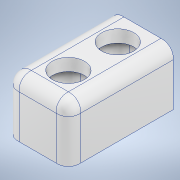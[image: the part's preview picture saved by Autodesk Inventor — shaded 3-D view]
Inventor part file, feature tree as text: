
AUTODESK INVENTOR PART (.ipt)
format: ipt  version: 2021 (Build 250183000, 183)  size: 1,595,392 bytes
history: native  units: in
note: dims shown in document units (in); Inventor stores cm internally (conversion verified against a paired STEP export)
features: extrude x9, other x7, fillet x2, sketch x1
ambient origin geometry x8: Origin, YZ Plane, XZ Plane, XY Plane, X Axis, Y Axis, Z Axis, Center Point
bodies: Body1 (feature_tree)
feature tree (19):
  extrude  "Base"  Depth=1.9685in
  extrude  "Top"  Depth=1.7717in TaperAngle=0.0deg
  extrude  "Walls"  Depth=1.1811in
  fillet  "Outer"  Radius=1.1811in
  extrude  "Wire"  Depth=1.1811in
  extrude  "Wall Holes"  Depth=1.1811in
  extrude  "Text"  Depth=1.5748in
  extrude  "Extrusion9"  Depth=1.5748in
  fillet  "Inner Fillet"  Radius=1.5748in
  extrude  "Extrusion14"  Depth=0.7087in TaperAngle=0.0deg
  extrude  "Extrusion16"  Depth=0.315in
  other  "Base Sketch"
  other  "Top Sketch"
  other  "Walls Sketch"
  other  "Wire Sketch"
  other  "Wall Holes Sketch"
  other  "Text Sketch"
  other  "Support"
  sketch  "Sketch25"  dims[d6=6.6929in d7=1.9685in d8=1.7717in d9=0.0in d10=1.1811in d11=1.1811in d12=1.1811in d13=1.1811in d14=1.5748in d15=1.5748in d16=1.5748in d19=0.7087in d20=0.0in d21=0.315in d22=0.315in d23=0.2362in d24=0.2362in d25=1.378in d26=0.0in d27=1.0236in d28=1.0236in d29=1.0236in d30=1.0236in d31=0.7874in d32=3.3465in d33=1.4961in d35=0.9843in d36=0.3937in d38=0.3937in d39=0.0in d52=0.315in d55=0.1969in d56=0.0in d58=0.3937in d65=0.315in d66=0.1575in d67=0.1575in d68=0.315in d69=0.2774in d70=0.2774in d71=0.0499in d72=0.0499in d73=0.0787in d74=0.0in d77=0.6496in d81=0.5906in d82=0.0in d85=0.4724in d86=0.1575in d87=0.1575in d88=0.9843in d89=0.315in d90=0.1575in d92=0.0in d93=0.1181in d94=0.0in d95=0.1575in d96=0.6496in d131=0.1969in d132=0.0in d143=0.0in d144=0.0in d145=0.0787in d146=0.1575in d151=0.2756in d152=0.0in d153=0.2756in d154=0.0in d155=3.3465in d156=0.0in d44=0.0197in d45=0.0344in d46=0.0197in d47=0.0344in d48=0.0197in d49=0.0344in d59=0.0197in d60=0.0344in d61=0.0197in d62=0.0344in]
